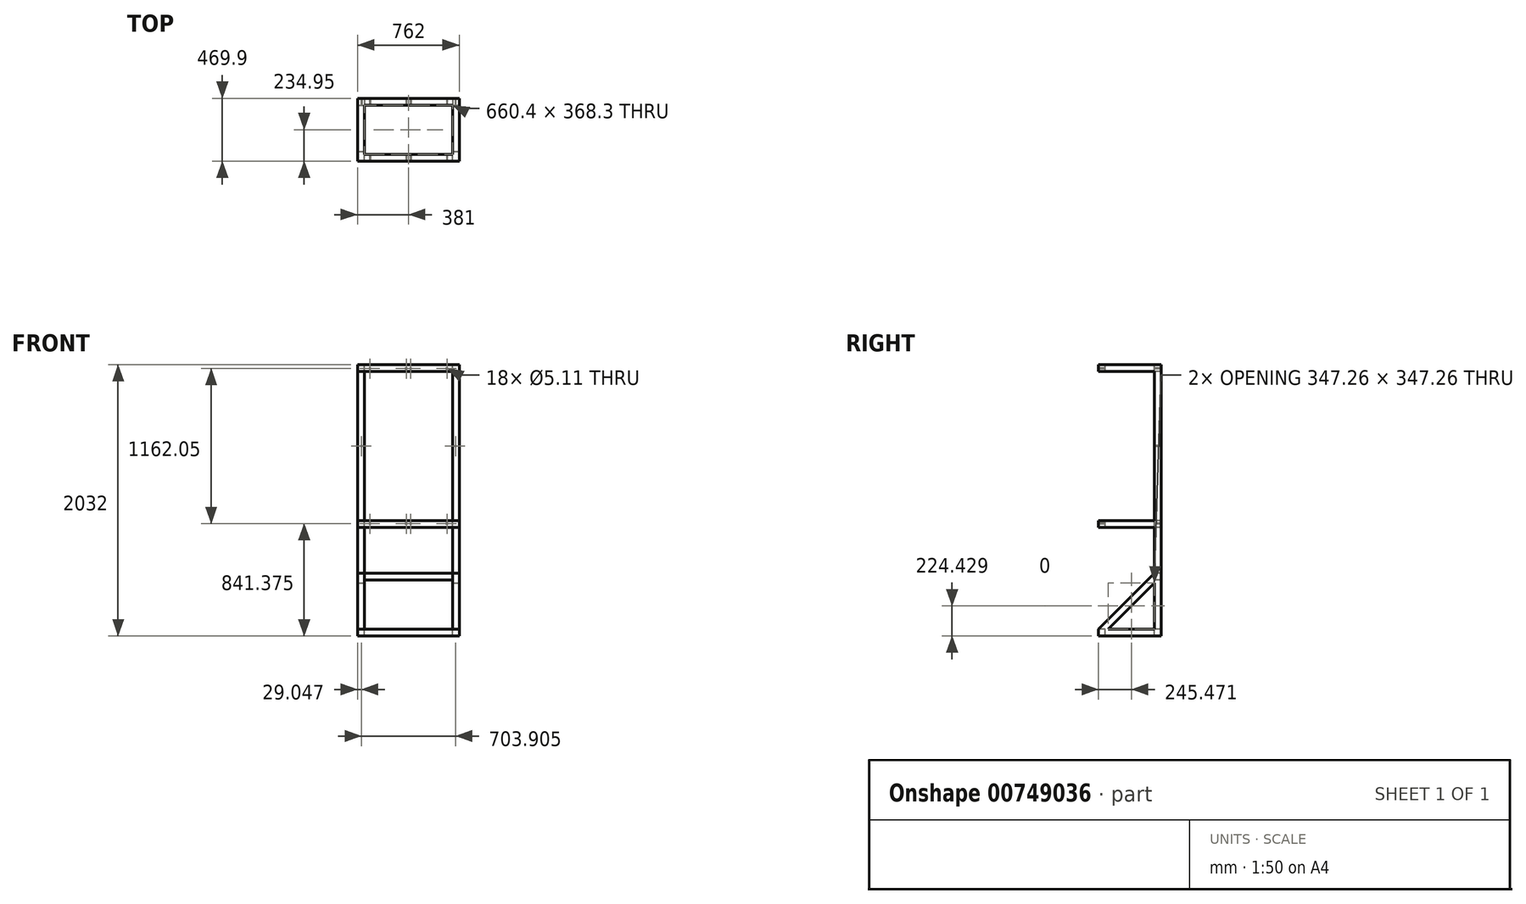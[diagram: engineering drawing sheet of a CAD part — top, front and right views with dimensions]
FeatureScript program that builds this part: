
annotation { "Feature Type Name" : "Feature", "Feature Type Description" : "" }
export const myFeature = defineFeature(function(context is Context, id is Id, definition is map)
    precondition{}
    {
        {
            var Q0;
            Q0=qCreatedBy(makeId("Front.planeOp"),FACE);
            var sketch = newSketch(context, id + "F0", { "sketchPlane" : qUnion([Q0])});
            skLineSegment(sketch, "E0.bottom", {"start": v(0, 0) * mm, "end": v(762, 0) * mm});
            skLineSegment(sketch, "E0.top", {"start": v(0, 2032) * mm, "end": v(762, 2032) * mm});
            skLineSegment(sketch, "E0.left", {"start": v(0, 0) * mm, "end": v(0, 2032) * mm});
            skLineSegment(sketch, "E0.right", {"start": v(762, 0) * mm, "end": v(762, 2032) * mm});
            skSolve(sketch);
        }
        {
            var Q0;
            Q0 = qSketchRegion(id + "F0", true);
            extrude(context, id + "F1", {"entities" : qUnion([Q0]), "depth" : 469.9 * mm, "offsetDistance" : 25.4 * mm});
        }
        {
            var Q0;
            Q0=makeQuery(id+"F1.opExtrude","SWEPT_FACE",FACE,{"disambiguationData":[OSD([sQuery(id+"F0.wireOp",EDGE,"E0.right")])]});
            var sketch = newSketch(context, id + "F2", { "sketchPlane" : qUnion([Q0])});
            skLineSegment(sketch, "E1.bottom", {"start": v(-469.9, 1981.2) * mm, "end": v(-50.8, 1981.2) * mm});
            skLineSegment(sketch, "E1.top", {"start": v(-469.9, 863.6) * mm, "end": v(-50.8, 863.6) * mm});
            skLineSegment(sketch, "E1.left", {"start": v(-469.9, 1981.2) * mm, "end": v(-469.9, 863.6) * mm});
            skLineSegment(sketch, "E1.right", {"start": v(-50.8, 1981.2) * mm, "end": v(-50.8, 863.6) * mm});
            skLineSegment(sketch, "E2", {"start": v(-469.9, 812.8) * mm, "end": v(-50.8, 812.8) * mm});
            skLineSegment(sketch, "E3", {"start": v(-50.8, 812.8) * mm, "end": v(-50.8, 469.9) * mm});
            skLineSegment(sketch, "E4", {"start": v(-50.8, 469.9) * mm, "end": v(-469.9, 50.8) * mm});
            skLineSegment(sketch, "E5", {"start": v(-50.8, 398.06) * mm, "end": v(-50.8, 50.8) * mm});
            skLineSegment(sketch, "E6", {"start": v(-50.8, 50.8) * mm, "end": v(-398.06, 50.8) * mm});
            skLineSegment(sketch, "E7", {"start": v(-398.06, 50.8) * mm, "end": v(-50.8, 398.06) * mm});
            skSolve(sketch);
        }
        {
            var Q0;
            Q0 = qSketchRegion(id + "F2", true);
            var Q1;
            {var subQ0=sQuery(id+"F2.wireOp",EDGE,"E2");Q1=makeQuery(id+"F2.imprint","IMPRINT",FACE,{"disambiguationData":[TD([[makeQuery(id+"F2.imprint","IMPRINT",EDGE,{"derivedFrom":subQ0}),-1.0]])]});}
            extrude(context, id + "F3", {"entities" : qUnion([Q0, Q1]), "operationType" : NewBodyOperationType.REMOVE, "oppositeDirection" : true, "depth" : 762 * mm, "offsetDistance" : 25.4 * mm});
        }
        {
            var Q0;
            Q0=makeQuery(id+"F1.opExtrude","SWEPT_FACE",FACE,{"disambiguationData":[OSD([sQuery(id+"F0.wireOp",EDGE,"E0.top")])]});
            var sketch = newSketch(context, id + "F4", { "sketchPlane" : qUnion([Q0])});
            skLineSegment(sketch, "E8.bottom", {"start": v(50.8, -419.1) * mm, "end": v(711.2, -419.1) * mm});
            skLineSegment(sketch, "E8.top", {"start": v(50.8, -50.8) * mm, "end": v(711.2, -50.8) * mm});
            skLineSegment(sketch, "E8.left", {"start": v(50.8, -419.1) * mm, "end": v(50.8, -50.8) * mm});
            skLineSegment(sketch, "E8.right", {"start": v(711.2, -419.1) * mm, "end": v(711.2, -50.8) * mm});
            skSolve(sketch);
        }
        {
            var Q0;
            Q0 = qSketchRegion(id + "F4", true);
            extrude(context, id + "F5", {"entities" : qUnion([Q0]), "operationType" : NewBodyOperationType.REMOVE, "oppositeDirection" : true, "depth" : 2133.6 * mm, "offsetDistance" : 25.4 * mm});
        }
        {
            var Q0;
            Q0=makeQuery(id+"F5.boolean.opBoolean","MERGE",FACE,{"derivedFrom":[makeQuery(id+"F3.boolean.opBoolean","COPY",FACE,{"derivedFrom":makeQuery(id+"F3.opExtrude","SWEPT_FACE",FACE,{"disambiguationData":[OSD([sQuery(id+"F2.wireOp",EDGE,"E1.right")])]})}),makeQuery(id+"F3.boolean.opBoolean","COPY",FACE,{"derivedFrom":makeQuery(id+"F3.opExtrude","SWEPT_FACE",FACE,{"disambiguationData":[OSD([sQuery(id+"F2.wireOp",EDGE,"E3")])]})}),makeQuery(id+"F3.boolean.opBoolean","COPY",FACE,{"derivedFrom":makeQuery(id+"F3.opExtrude","SWEPT_FACE",FACE,{"disambiguationData":[OSD([sQuery(id+"F2.wireOp",EDGE,"E5")])]})})],"fromTools":[makeQuery(id+"F5.opExtrude","SWEPT_FACE",FACE,{"disambiguationData":[OSD([sQuery(id+"F4.wireOp",EDGE,"E8.top")])]})]});
            var sketch = newSketch(context, id + "F6", { "sketchPlane" : qUnion([Q0])});
            skLineSegment(sketch, "E9.bottom", {"start": v(50.8, 1981.2) * mm, "end": v(711.2, 1981.2) * mm});
            skLineSegment(sketch, "E9.top", {"start": v(50.8, 863.6) * mm, "end": v(711.2, 863.6) * mm});
            skLineSegment(sketch, "E9.left", {"start": v(50.8, 1981.2) * mm, "end": v(50.8, 863.6) * mm});
            skLineSegment(sketch, "E9.right", {"start": v(711.2, 1981.2) * mm, "end": v(711.2, 863.6) * mm});
            skLineSegment(sketch, "E10.bottom", {"start": v(50.8, 812.8) * mm, "end": v(711.2, 812.8) * mm});
            skLineSegment(sketch, "E10.top", {"start": v(50.8, 469.9) * mm, "end": v(711.2, 469.9) * mm});
            skLineSegment(sketch, "E10.left", {"start": v(50.8, 812.8) * mm, "end": v(50.8, 469.9) * mm});
            skLineSegment(sketch, "E10.right", {"start": v(711.2, 812.8) * mm, "end": v(711.2, 469.9) * mm});
            skPoint(sketch, "E11.firstSnap0", {"position": v(50.8, 433.98) * mm});
            skLineSegment(sketch, "E11.bottom", {"start": v(50.8, 419.1) * mm, "end": v(711.2, 419.1) * mm});
            skLineSegment(sketch, "E11.top", {"start": v(50.8, 50.8) * mm, "end": v(711.2, 50.8) * mm});
            skLineSegment(sketch, "E11.left", {"start": v(50.8, 419.1) * mm, "end": v(50.8, 50.8) * mm});
            skLineSegment(sketch, "E11.right", {"start": v(711.2, 419.1) * mm, "end": v(711.2, 50.8) * mm});
            skSolve(sketch);
        }
        {
            var Q0;
            Q0 = qSketchRegion(id + "F6", true);
            extrude(context, id + "F7", {"entities" : qUnion([Q0]), "operationType" : NewBodyOperationType.REMOVE, "endBound" : BoundingType.THROUGH_ALL, "oppositeDirection" : true, "depth" : 50.8 * mm, "offsetDistance" : 25.4 * mm});
        }
        {
            var Q0;
            {var subQ0=sQuery(id+"F0.wireOp",EDGE,"E0.bottom");var subQ1=sQuery(id+"F0.wireOp",EDGE,"E0.right");var subQ2=sQuery(id+"F0.wireOp",EDGE,"E0.left");Q0=makeQuery(id+"F3.boolean.opBoolean","SPLIT",FACE,{"disambiguationData":[TD([makeQuery(id+"F1.opExtrude","SWEPT_FACE",FACE,{"disambiguationData":[OSD([subQ0])]})])],"derivedFrom":makeQuery(id+"F1.opExtrude","CAP_FACE",FACE,{"disambiguationData":[OSD([subQ0,sQuery(id+"F0.wireOp",EDGE,"E0.top"),subQ2,subQ1])],"isStart":false})});}
            var sketch = newSketch(context, id + "F8", { "sketchPlane" : qUnion([Q0])});
            skLineSegment(sketch, "E12.bottom", {"start": v(50.8, 50.8) * mm, "end": v(711.2, 50.8) * mm});
            skLineSegment(sketch, "E12.top", {"start": v(50.8, 101.6) * mm, "end": v(711.2, 101.6) * mm});
            skLineSegment(sketch, "E12.left", {"start": v(50.8, 50.8) * mm, "end": v(50.8, 101.6) * mm});
            skLineSegment(sketch, "E12.right", {"start": v(711.2, 50.8) * mm, "end": v(711.2, 101.6) * mm});
            skSolve(sketch);
        }
        {
            var Q0;
            Q0 = qSketchRegion(id + "F8", true);
            extrude(context, id + "F9", {"entities" : qUnion([Q0]), "operationType" : NewBodyOperationType.REMOVE, "oppositeDirection" : true, "depth" : 50.8 * mm, "offsetDistance" : 25.4 * mm});
        }
        {
            var Q0;
            Q0=makeQuery(id+"F1.opExtrude","CAP_FACE",FACE,{"disambiguationData":[OSD([sQuery(id+"F0.wireOp",EDGE,"E0.bottom"),sQuery(id+"F0.wireOp",EDGE,"E0.top"),sQuery(id+"F0.wireOp",EDGE,"E0.left"),sQuery(id+"F0.wireOp",EDGE,"E0.right")])],"isStart":true});
            var sketch = newSketch(context, id + "F10", { "sketchPlane" : qUnion([Q0])});
            skLineSegment(sketch, "E13", {"start": v(-762, 1422.4) * mm, "end": v(0, 1422.4) * mm, "construction": true});
            skPoint(sketch, "E13.startSnap0", {"position": v(-711.2, 1422.4) * mm});
            skLineSegment(sketch, "E14", {"start": v(-381, 2032) * mm, "end": v(-381, 812.8) * mm, "construction": true});
            skLineSegment(sketch, "E15", {"start": v(-711.2, 2032) * mm, "end": v(-359.25, 1422.4) * mm, "construction": true});
            skLineSegment(sketch, "E16", {"start": v(-711.2, 2032) * mm, "end": v(-355.6, 2032) * mm, "construction": true});
            skLineSegment(sketch, "E17", {"start": v(-355.6, 2032) * mm, "end": v(-3.65, 1422.4) * mm, "construction": true});
            skLineSegment(sketch, "E18", {"start": v(-694.7, 2003.42) * mm, "end": v(-339.1, 2003.42) * mm, "construction": true});
            skLineSegment(sketch, "E19", {"start": v(-685.8, 2032) * mm, "end": v(-333.85, 1422.4) * mm, "construction": true});
            skLineSegment(sketch, "E20", {"start": v(-381, 2032) * mm, "end": v(-29.05, 1422.4) * mm, "construction": true});
            skPoint(sketch, "E21", {"position": v(-669.3, 2003.42) * mm});
            skPoint(sketch, "E22", {"position": v(-364.5, 2003.43) * mm});
            skPoint(sketch, "E23", {"position": v(-333.85, 1422.4) * mm});
            skPoint(sketch, "E24", {"position": v(-29.05, 1422.4) * mm});
            skPoint(sketch, "E25.MirrorP", {"position": v(-428.15, 1422.4) * mm});
            skPoint(sketch, "E26.MirrorP", {"position": v(-732.95, 1422.4) * mm});
            skPoint(sketch, "E27.MirrorP", {"position": v(-397.5, 2003.43) * mm});
            skPoint(sketch, "E28.MirrorP", {"position": v(-92.7, 2003.42) * mm});
            skPoint(sketch, "E29.MirrorP", {"position": v(-669.3, 841.38) * mm});
            skPoint(sketch, "E30.MirrorP", {"position": v(-397.5, 841.37) * mm});
            skPoint(sketch, "E31.MirrorP", {"position": v(-364.5, 841.37) * mm});
            skPoint(sketch, "E32.MirrorP", {"position": v(-92.7, 841.38) * mm});
            skSolve(sketch);
        }
        {
            var Q0;
            Q0=sQuery(id+"F10.wireOp",VERTEX,"E27.MirrorP");
            var Q1;
            Q1=sQuery(id+"F10.wireOp",VERTEX,"E22");
            var Q2;
            Q2=sQuery(id+"F10.wireOp",VERTEX,"E28.MirrorP");
            var Q3;
            Q3=sQuery(id+"F10.wireOp",VERTEX,"E24");
            var Q4;
            Q4=sQuery(id+"F10.wireOp",VERTEX,"E26.MirrorP");
            var Q5;
            Q5=sQuery(id+"F10.wireOp",VERTEX,"E29.MirrorP");
            var Q6;
            Q6=sQuery(id+"F10.wireOp",VERTEX,"E30.MirrorP");
            var Q7;
            Q7=sQuery(id+"F10.wireOp",VERTEX,"E31.MirrorP");
            var Q8;
            Q8=sQuery(id+"F10.wireOp",VERTEX,"E32.MirrorP");
            var Q9;
            Q9=sQuery(id+"F10.wireOp",VERTEX,"E21");
            var Q10;
            Q10=makeQuery(id+"F1.opExtrude","SWEPT_BODY",BODY,{"disambiguationData":[OSD([sQuery(id+"F0.wireOp",EDGE,"E0.bottom"),sQuery(id+"F0.wireOp",EDGE,"E0.top"),sQuery(id+"F0.wireOp",EDGE,"E0.left"),sQuery(id+"F0.wireOp",EDGE,"E0.right")])]});
            hole(context, id + "F11", {"style" : HoleStyle.SIMPLE, "endStyle" : HoleEndStyle.THROUGH, "standardTappedOrClearance" : lookupTablePath({ "standard" : "ANSI", "engagement" : "75%", "pitch" : "20 tpi", "size" : "1/4", "type" : "Tapped" }), "standardBlindInLast" : lookupTablePath({ "standard" : "ANSI", "fit" : "Normal", "engagement" : "75%", "pitch" : "20 tpi", "size" : "1/4", "type" : "Clearance & tapped" }), "holeDiameter" : 5.1 * mm, "majorDiameter" : 6.35 * mm, "showTappedDepth" : true, "isTappedThrough" : true, "tappedDepth" : 22.25 * mm, "tapClearance" : 3, "locations" : qUnion([Q0, Q1, Q2, Q3, Q4, Q5, Q6, Q7, Q8, Q9]), "scope" : qUnion([Q10])});
        }
    });
